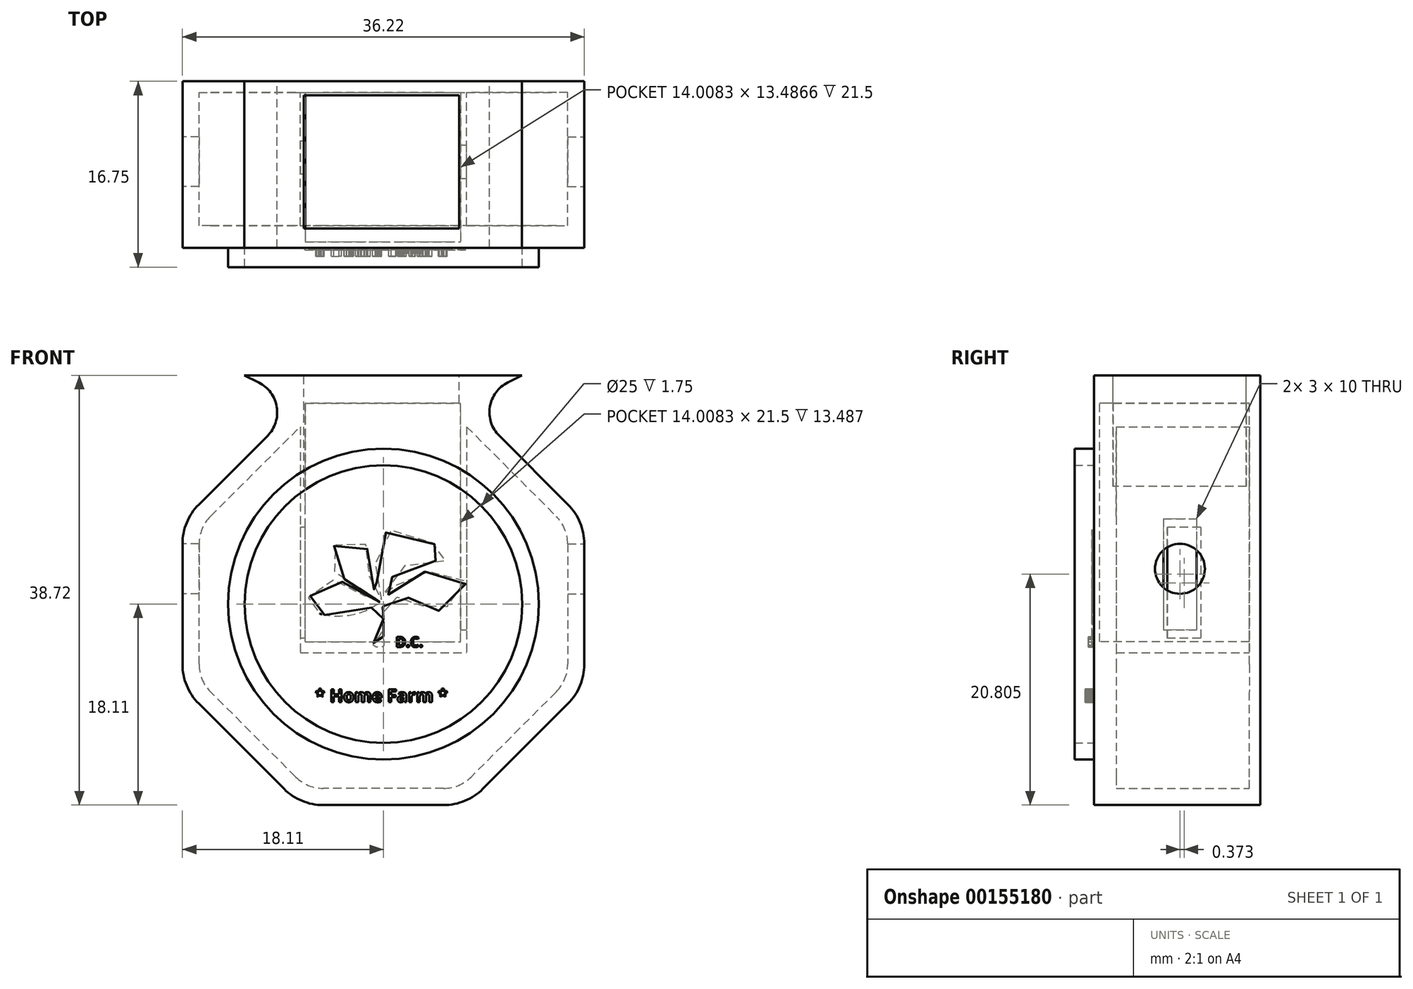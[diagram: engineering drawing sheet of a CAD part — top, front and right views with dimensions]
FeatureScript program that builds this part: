
annotation { "Feature Type Name" : "Feature", "Feature Type Description" : "" }
export const myFeature = defineFeature(function(context is Context, id is Id, definition is map)
    precondition{}
    {
        {
            var Q0;
            Q0=qCreatedBy(makeId("Front.planeOp"),FACE);
            var sketch = newSketch(context, id + "F0", { "sketchPlane" : qUnion([Q0])});
            skCircle(sketch, "E0.cCircle", {"center": v(0, 0) * mm, "radius": 18.1 * mm, "construction": true});
            skLineSegment(sketch, "E0.0", {"start": v(5.43, -18.1) * mm, "end": v(-5.43, -18.1) * mm});
            skLineSegment(sketch, "E0.1", {"start": v(-8.96, -16.64) * mm, "end": v(-16.64, -8.96) * mm});
            skLineSegment(sketch, "E0.2", {"start": v(-18.1, -5.43) * mm, "end": v(-18.1, 5.43) * mm});
            skLineSegment(sketch, "E0.3", {"start": v(-16.64, 8.96) * mm, "end": v(-7.5, 18.1) * mm});
            skLineSegment(sketch, "E0.4", {"start": v(-7.5, 18.1) * mm, "end": v(7.5, 18.1) * mm});
            skLineSegment(sketch, "E0.5", {"start": v(7.5, 18.1) * mm, "end": v(16.64, 8.96) * mm});
            skLineSegment(sketch, "E0.6", {"start": v(18.1, 5.43) * mm, "end": v(18.1, -5.43) * mm});
            skLineSegment(sketch, "E0.7", {"start": v(16.64, -8.96) * mm, "end": v(8.96, -16.64) * mm});
            skPoint(sketch, "E0.0.midPoint", {"position": v(0, -18.1) * mm});
            skPoint(sketch, "E1.visualSharp", {"position": v(7.5, -18.1) * mm});
            skArc(sketch, "E1.filletArc", {"start": v(5.43, -18.1) * mm, "mid": v(7.34, -17.73) * mm, "end": v(8.96, -16.64) * mm});
            skPoint(sketch, "E2.visualSharp", {"position": v(-7.5, -18.1) * mm});
            skArc(sketch, "E2.filletArc", {"start": v(-8.96, -16.64) * mm, "mid": v(-7.34, -17.73) * mm, "end": v(-5.43, -18.1) * mm});
            skPoint(sketch, "E3.visualSharp", {"position": v(-18.1, -7.5) * mm});
            skArc(sketch, "E3.filletArc", {"start": v(-18.1, -5.43) * mm, "mid": v(-17.73, -7.34) * mm, "end": v(-16.64, -8.96) * mm});
            skPoint(sketch, "E4.visualSharp", {"position": v(18.1, -7.5) * mm});
            skArc(sketch, "E4.filletArc", {"start": v(16.64, -8.96) * mm, "mid": v(17.73, -7.34) * mm, "end": v(18.1, -5.43) * mm});
            skPoint(sketch, "E5.visualSharp", {"position": v(18.1, 7.5) * mm});
            skArc(sketch, "E5.filletArc", {"start": v(18.1, 5.43) * mm, "mid": v(17.73, 7.34) * mm, "end": v(16.64, 8.96) * mm});
            skPoint(sketch, "E6.visualSharp", {"position": v(-18.1, 7.5) * mm});
            skArc(sketch, "E6.filletArc", {"start": v(-16.64, 8.96) * mm, "mid": v(-17.73, 7.34) * mm, "end": v(-18.1, 5.43) * mm});
            skLineSegment(sketch, "E7.0", {"start": v(-15.72, 16.6) * mm, "end": v(4.28, 16.6) * mm});
            skSolve(sketch);
        }
        {
            var Q0;
            Q0=makeQuery(id+"F0.imprint","IMPRINT",FACE,{"disambiguationData":[TD([[makeQuery(id+"F0.imprint","IMPRINT",EDGE,{"derivedFrom":sQuery(id+"F0.wireOp",EDGE,"E0.0")}),-1.0]])]});
            extrude(context, id + "F1", {"entities" : qUnion([Q0]), "depth" : 15 * mm});
        }
        {
            var Q0;
            Q0=makeQuery(id+"F1.opExtrude","CAP_FACE",FACE,{"disambiguationData":[OSD([sQuery(id+"F0.wireOp",EDGE,"E0.0"),sQuery(id+"F0.wireOp",EDGE,"E0.1"),sQuery(id+"F0.wireOp",EDGE,"E0.2"),sQuery(id+"F0.wireOp",EDGE,"E0.3"),sQuery(id+"F0.wireOp",EDGE,"E0.4"),sQuery(id+"F0.wireOp",EDGE,"E0.5"),sQuery(id+"F0.wireOp",EDGE,"E0.6"),sQuery(id+"F0.wireOp",EDGE,"E0.7"),sQuery(id+"F0.wireOp",EDGE,"E1.filletArc"),sQuery(id+"F0.wireOp",EDGE,"E2.filletArc"),sQuery(id+"F0.wireOp",EDGE,"E3.filletArc"),sQuery(id+"F0.wireOp",EDGE,"E4.filletArc"),sQuery(id+"F0.wireOp",EDGE,"E5.filletArc"),sQuery(id+"F0.wireOp",EDGE,"E6.filletArc")])],"isStart":false});
            var sketch = newSketch(context, id + "F2", { "sketchPlane" : qUnion([Q0])});
            skCircle(sketch, "E8", {"center": v(0, 0) * mm, "radius": 14 * mm});
            skCircle(sketch, "E9.0", {"center": v(0, 0) * mm, "radius": 12.5 * mm});
            skSolve(sketch);
        }
        {
            var Q0;
            Q0 = qSketchRegion(id + "F2", true);
            extrude(context, id + "F3", {"entities" : qUnion([Q0]), "operationType" : NewBodyOperationType.ADD, "depth" : 1.75 * mm});
        }
        {
            var Q0;
            Q0=makeQuery(id+"F3.boolean.opBoolean","SPLIT",FACE,{"disambiguationData":[TD([makeQuery(id+"F3.opExtrude","SWEPT_FACE",FACE,{"disambiguationData":[OSD([sQuery(id+"F2.wireOp",EDGE,"E9.0")])]})])],"derivedFrom":makeQuery(id+"F1.opExtrude","CAP_FACE",FACE,{"disambiguationData":[OSD([sQuery(id+"F0.wireOp",EDGE,"E0.0"),sQuery(id+"F0.wireOp",EDGE,"E0.1"),sQuery(id+"F0.wireOp",EDGE,"E0.2"),sQuery(id+"F0.wireOp",EDGE,"E0.3"),sQuery(id+"F0.wireOp",EDGE,"E0.4"),sQuery(id+"F0.wireOp",EDGE,"E0.5"),sQuery(id+"F0.wireOp",EDGE,"E0.6"),sQuery(id+"F0.wireOp",EDGE,"E0.7"),sQuery(id+"F0.wireOp",EDGE,"E1.filletArc"),sQuery(id+"F0.wireOp",EDGE,"E2.filletArc"),sQuery(id+"F0.wireOp",EDGE,"E3.filletArc"),sQuery(id+"F0.wireOp",EDGE,"E4.filletArc"),sQuery(id+"F0.wireOp",EDGE,"E5.filletArc"),sQuery(id+"F0.wireOp",EDGE,"E6.filletArc")])],"isStart":false})});
            var sketch = newSketch(context, id + "F4", { "sketchPlane" : qUnion([Q0])});
            skText(sketch, "E10", { "text": "* Home Farm *", "fontName": "OpenSans-Bold.ttf"});
            const initialGuessF4  = {"E10": [-0.00615, -0.00883, 1, 0, 0.00116]};
            skSetInitialGuess(sketch, initialGuessF4);
            skSolve(sketch);
        }
        {
            var Q0;
            Q0 = qSketchRegion(id + "F4", true);
            extrude(context, id + "F5", {"entities" : qUnion([Q0]), "operationType" : NewBodyOperationType.ADD, "depth" : 0.78 * mm});
        }
        {
            var Q0;
            Q0=makeQuery(id+"F1.opExtrude","SWEPT_FACE",FACE,{"disambiguationData":[OSD([sQuery(id+"F0.wireOp",EDGE,"E0.4")])]});
            var sketch = newSketch(context, id + "F6", { "sketchPlane" : qUnion([Q0])});
            skLineSegment(sketch, "E11.bottom", {"start": v(-7.5, 0) * mm, "end": v(7.5, 0) * mm});
            skLineSegment(sketch, "E11.top", {"start": v(-7.5, -15) * mm, "end": v(7.5, -15) * mm});
            skLineSegment(sketch, "E11.left", {"start": v(-7.5, 0) * mm, "end": v(-7.5, -15) * mm});
            skLineSegment(sketch, "E11.right", {"start": v(7.5, 0) * mm, "end": v(7.5, -15) * mm});
            skSolve(sketch);
        }
        {
            var Q0;
            {var subQ0=makeQuery(id+"F3.opExtrude","SWEPT_FACE",FACE,{"disambiguationData":[OSD([sQuery(id+"F2.wireOp",EDGE,"E9.0")])]});Q0=makeQuery(id+"F5.boolean.opBoolean","SPLIT",FACE,{"disambiguationData":[TD([subQ0])],"derivedFrom":makeQuery(id+"F3.boolean.opBoolean","SPLIT",FACE,{"disambiguationData":[TD([subQ0])],"derivedFrom":makeQuery(id+"F1.opExtrude","CAP_FACE",FACE,{"disambiguationData":[OSD([sQuery(id+"F0.wireOp",EDGE,"E0.0"),sQuery(id+"F0.wireOp",EDGE,"E0.1"),sQuery(id+"F0.wireOp",EDGE,"E0.2"),sQuery(id+"F0.wireOp",EDGE,"E0.3"),sQuery(id+"F0.wireOp",EDGE,"E0.4"),sQuery(id+"F0.wireOp",EDGE,"E0.5"),sQuery(id+"F0.wireOp",EDGE,"E0.6"),sQuery(id+"F0.wireOp",EDGE,"E0.7"),sQuery(id+"F0.wireOp",EDGE,"E1.filletArc"),sQuery(id+"F0.wireOp",EDGE,"E2.filletArc"),sQuery(id+"F0.wireOp",EDGE,"E3.filletArc"),sQuery(id+"F0.wireOp",EDGE,"E4.filletArc"),sQuery(id+"F0.wireOp",EDGE,"E5.filletArc"),sQuery(id+"F0.wireOp",EDGE,"E6.filletArc")])],"isStart":false})})});}
            var sketch = newSketch(context, id + "F7", { "sketchPlane" : qUnion([Q0])});
            skFitSpline(sketch, "E12", {"points": [v(0, -2.92) * mm, v(0.28, -1.42) * mm, v(0, 0) * mm, v(1.05, 0.6) * mm, v(2.74, 0.4) * mm, v(4.44, -0.62) * mm, v(6.04, 0) * mm, v(7.38, 2) * mm, v(4.3, 2.93) * mm, v(1.37, 1.93) * mm, v(0, 0.4) * mm, v(0.55, 2.06) * mm, v(3.22, 3.86) * mm, v(6.04, 4.07) * mm, v(3.24, 6.14) * mm, v(0, 6.25) * mm, v(-0.59, 1.86) * mm, v(-0.2, 0.4) * mm, v(-1.13, 2) * mm, v(-1.4, 4.68) * mm, v(-2.23, 5.91) * mm, v(-5.16, 4.48) * mm, v(-3.39, 2.18) * mm, v(-0.27, 0.2) * mm, v(-1.68, 0.74) * mm, v(-4.41, 2.18) * mm, v(-6.33, 0.97) * mm, v(-7.08, 0) * mm, v(-4.96, -1.03) * mm, v(-1.23, -0.42) * mm, v(-0.34, 0) * mm, v(0, -1.1) * mm, v(0, -1.62) * mm, v(-0.31, -2.8) * mm, v(-0.93, -3.7) * mm, v(0, -3.81) * mm, v(0, -2.92) * mm]});
            skSolve(sketch);
        }
        {
            var Q0;
            Q0=makeQuery(id+"F7.imprint","IMPRINT",FACE,{"disambiguationData":[TD([[makeQuery(id+"F7.imprint","IMPRINT",EDGE,{"derivedFrom":sQuery(id+"F7.wireOp",EDGE,"E12")}),1.0]])]});
            extrude(context, id + "F8", {"entities" : qUnion([Q0]), "operationType" : NewBodyOperationType.ADD, "depth" : 0.2 * mm});
        }
        {
            var Q0;
            {var subQ0=makeQuery(id+"F3.opExtrude","SWEPT_FACE",FACE,{"disambiguationData":[OSD([sQuery(id+"F2.wireOp",EDGE,"E9.0")])]});Q0=makeQuery(id+"F5.boolean.opBoolean","SPLIT",FACE,{"disambiguationData":[TD([subQ0])],"derivedFrom":makeQuery(id+"F3.boolean.opBoolean","SPLIT",FACE,{"disambiguationData":[TD([subQ0])],"derivedFrom":makeQuery(id+"F1.opExtrude","CAP_FACE",FACE,{"disambiguationData":[OSD([sQuery(id+"F0.wireOp",EDGE,"E0.0"),sQuery(id+"F0.wireOp",EDGE,"E0.1"),sQuery(id+"F0.wireOp",EDGE,"E0.2"),sQuery(id+"F0.wireOp",EDGE,"E0.3"),sQuery(id+"F0.wireOp",EDGE,"E0.4"),sQuery(id+"F0.wireOp",EDGE,"E0.5"),sQuery(id+"F0.wireOp",EDGE,"E0.6"),sQuery(id+"F0.wireOp",EDGE,"E0.7"),sQuery(id+"F0.wireOp",EDGE,"E1.filletArc"),sQuery(id+"F0.wireOp",EDGE,"E2.filletArc"),sQuery(id+"F0.wireOp",EDGE,"E3.filletArc"),sQuery(id+"F0.wireOp",EDGE,"E4.filletArc"),sQuery(id+"F0.wireOp",EDGE,"E5.filletArc"),sQuery(id+"F0.wireOp",EDGE,"E6.filletArc")])],"isStart":false})})});}
            var sketch = newSketch(context, id + "F9", { "sketchPlane" : qUnion([Q0])});
            skText(sketch, "E13", { "text": "D.C.", "fontName": "OpenSans-Bold.ttf"});
            const initialGuessF9  = {"E13": [0.00109, -0.00387, 1, 0, 0.00092]};
            skSetInitialGuess(sketch, initialGuessF9);
            skSolve(sketch);
        }
        {
            var Q0;
            Q0 = qSketchRegion(id + "F9", true);
            extrude(context, id + "F10", {"entities" : qUnion([Q0]), "operationType" : NewBodyOperationType.ADD, "depth" : 0.5 * mm});
        }
        {
            var Q0;
            Q0=makeQuery(id+"F1.opExtrude","CAP_FACE",FACE,{"disambiguationData":[OSD([sQuery(id+"F0.wireOp",EDGE,"E0.0"),sQuery(id+"F0.wireOp",EDGE,"E0.1"),sQuery(id+"F0.wireOp",EDGE,"E0.2"),sQuery(id+"F0.wireOp",EDGE,"E0.3"),sQuery(id+"F0.wireOp",EDGE,"E0.4"),sQuery(id+"F0.wireOp",EDGE,"E0.5"),sQuery(id+"F0.wireOp",EDGE,"E0.6"),sQuery(id+"F0.wireOp",EDGE,"E0.7"),sQuery(id+"F0.wireOp",EDGE,"E1.filletArc"),sQuery(id+"F0.wireOp",EDGE,"E2.filletArc"),sQuery(id+"F0.wireOp",EDGE,"E3.filletArc"),sQuery(id+"F0.wireOp",EDGE,"E4.filletArc"),sQuery(id+"F0.wireOp",EDGE,"E5.filletArc"),sQuery(id+"F0.wireOp",EDGE,"E6.filletArc")])],"isStart":true});
            var sketch = newSketch(context, id + "F11", { "sketchPlane" : qUnion([Q0])});
            skArc(sketch, "E14.0", {"start": v(-7.9, -15.58) * mm, "mid": v(-6.77, -16.34) * mm, "end": v(-5.43, -16.6) * mm});
            skLineSegment(sketch, "E14.1", {"start": v(-15.58, -7.9) * mm, "end": v(-7.9, -15.58) * mm});
            skArc(sketch, "E14.2", {"start": v(-16.6, -5.43) * mm, "mid": v(-16.34, -6.77) * mm, "end": v(-15.58, -7.9) * mm});
            skLineSegment(sketch, "E14.3", {"start": v(16.6, -5.43) * mm, "end": v(16.6, 5.43) * mm});
            skArc(sketch, "E14.4", {"start": v(15.58, -7.9) * mm, "mid": v(16.34, -6.77) * mm, "end": v(16.6, -5.43) * mm});
            skLineSegment(sketch, "E14.5", {"start": v(7.9, -15.58) * mm, "end": v(15.58, -7.9) * mm});
            skArc(sketch, "E14.6", {"start": v(5.43, -16.6) * mm, "mid": v(6.77, -16.34) * mm, "end": v(7.9, -15.58) * mm});
            skArc(sketch, "E14.7", {"start": v(16.6, 5.43) * mm, "mid": v(16.34, 6.77) * mm, "end": v(15.58, 7.9) * mm});
            skLineSegment(sketch, "E14.8", {"start": v(15.58, 7.9) * mm, "end": v(6.88, 16.6) * mm});
            skLineSegment(sketch, "E14.9", {"start": v(6.88, 16.6) * mm, "end": v(-6.88, 16.6) * mm});
            skLineSegment(sketch, "E14.10", {"start": v(-5.43, -16.6) * mm, "end": v(5.43, -16.6) * mm});
            skLineSegment(sketch, "E14.11", {"start": v(-6.88, 16.6) * mm, "end": v(-15.58, 7.9) * mm});
            skArc(sketch, "E14.12", {"start": v(-15.58, 7.9) * mm, "mid": v(-16.34, 6.77) * mm, "end": v(-16.6, 5.43) * mm});
            skLineSegment(sketch, "E14.13", {"start": v(-16.6, 5.43) * mm, "end": v(-16.6, -5.43) * mm});
            skSolve(sketch);
        }
        {
            var Q0;
            Q0=makeQuery(id+"F11.imprint","IMPRINT",FACE,{"disambiguationData":[TD([[makeQuery(id+"F11.imprint","IMPRINT",EDGE,{"derivedFrom":sQuery(id+"F11.wireOp",EDGE,"E14.0")}),1.0]])]});
            extrude(context, id + "F12", {"entities" : qUnion([Q0]), "operationType" : NewBodyOperationType.REMOVE, "oppositeDirection" : true, "depth" : 13 * mm});
        }
        {
            var Q0;
            Q0=makeQuery(id+"F6.imprint","IMPRINT",FACE,{"disambiguationData":[TD([[makeQuery(id+"F6.imprint","IMPRINT",EDGE,{"derivedFrom":sQuery(id+"F6.wireOp",EDGE,"E11.bottom")}),-1.0]])]});
            extrude(context, id + "F13", {"entities" : qUnion([Q0]), "operationType" : NewBodyOperationType.ADD, "oppositeDirection" : true, "depth" : 22.5 * mm});
        }
        {
            var Q0;
            Q0=makeQuery(id+"F1.opExtrude","SWEPT_FACE",FACE,{"disambiguationData":[OSD([sQuery(id+"F0.wireOp",EDGE,"E0.4")])]});
            var sketch = newSketch(context, id + "F14", { "sketchPlane" : qUnion([Q0])});
            skLineSegment(sketch, "E15.bottom", {"start": v(-7.04, -0.51) * mm, "end": v(6.97, -0.51) * mm});
            skLineSegment(sketch, "E15.top", {"start": v(-7.04, -14.49) * mm, "end": v(6.97, -14.49) * mm});
            skLineSegment(sketch, "E15.left", {"start": v(-7.04, -0.51) * mm, "end": v(-7.04, -14.49) * mm});
            skLineSegment(sketch, "E15.right", {"start": v(6.97, -0.51) * mm, "end": v(6.97, -14.49) * mm});
            skSolve(sketch);
        }
        {
            var Q0;
            Q0=makeQuery(id+"F13.boolean.opBoolean","MERGE",FACE,{"derivedFrom":[makeQuery(id+"F1.opExtrude","CAP_FACE",FACE,{"disambiguationData":[OSD([sQuery(id+"F0.wireOp",EDGE,"E0.0"),sQuery(id+"F0.wireOp",EDGE,"E0.1"),sQuery(id+"F0.wireOp",EDGE,"E0.2"),sQuery(id+"F0.wireOp",EDGE,"E0.3"),sQuery(id+"F0.wireOp",EDGE,"E0.4"),sQuery(id+"F0.wireOp",EDGE,"E0.5"),sQuery(id+"F0.wireOp",EDGE,"E0.6"),sQuery(id+"F0.wireOp",EDGE,"E0.7"),sQuery(id+"F0.wireOp",EDGE,"E1.filletArc"),sQuery(id+"F0.wireOp",EDGE,"E2.filletArc"),sQuery(id+"F0.wireOp",EDGE,"E3.filletArc"),sQuery(id+"F0.wireOp",EDGE,"E4.filletArc"),sQuery(id+"F0.wireOp",EDGE,"E5.filletArc"),sQuery(id+"F0.wireOp",EDGE,"E6.filletArc")])],"isStart":true}),makeQuery(id+"F13.opExtrude","SWEPT_FACE",FACE,{"disambiguationData":[OSD([sQuery(id+"F6.wireOp",EDGE,"E11.bottom")])]})]});
            var sketch = newSketch(context, id + "F15", { "sketchPlane" : qUnion([Q0])});
            skLineSegment(sketch, "E16.bottom", {"start": v(-6.35, 12.73) * mm, "end": v(6.65, 12.73) * mm});
            skLineSegment(sketch, "E16.top", {"start": v(-6.35, 11.73) * mm, "end": v(6.65, 11.73) * mm});
            skLineSegment(sketch, "E16.left", {"start": v(-6.35, 12.73) * mm, "end": v(-6.35, 11.73) * mm});
            skLineSegment(sketch, "E16.right", {"start": v(6.65, 12.73) * mm, "end": v(6.65, 11.73) * mm});
            skLineSegment(sketch, "E17.bottom", {"start": v(-6.35, 9.52) * mm, "end": v(6.65, 9.52) * mm});
            skLineSegment(sketch, "E17.top", {"start": v(-6.35, 8.13) * mm, "end": v(6.65, 8.13) * mm});
            skLineSegment(sketch, "E17.left", {"start": v(-6.35, 9.52) * mm, "end": v(-6.35, 8.13) * mm});
            skLineSegment(sketch, "E17.right", {"start": v(6.65, 9.52) * mm, "end": v(6.65, 8.13) * mm});
            skLineSegment(sketch, "E18.bottom", {"start": v(-6.35, 5.8) * mm, "end": v(6.65, 5.8) * mm});
            skLineSegment(sketch, "E18.top", {"start": v(-6.35, 4.38) * mm, "end": v(6.65, 4.38) * mm});
            skLineSegment(sketch, "E18.left", {"start": v(-6.35, 5.8) * mm, "end": v(-6.35, 4.38) * mm});
            skLineSegment(sketch, "E18.right", {"start": v(6.65, 5.8) * mm, "end": v(6.65, 4.38) * mm});
            skLineSegment(sketch, "E19.bottom", {"start": v(-6.38, 2.26) * mm, "end": v(6.62, 2.26) * mm});
            skLineSegment(sketch, "E19.top", {"start": v(-6.38, 0.78) * mm, "end": v(6.62, 0.78) * mm});
            skLineSegment(sketch, "E19.left", {"start": v(-6.38, 2.26) * mm, "end": v(-6.38, 0.78) * mm});
            skLineSegment(sketch, "E19.right", {"start": v(6.62, 2.26) * mm, "end": v(6.62, 0.78) * mm});
            skLineSegment(sketch, "E20.bottom", {"start": v(-6.24, -1.06) * mm, "end": v(6.76, -1.06) * mm});
            skLineSegment(sketch, "E20.top", {"start": v(-6.24, -2.36) * mm, "end": v(6.76, -2.36) * mm});
            skLineSegment(sketch, "E20.left", {"start": v(-6.24, -1.06) * mm, "end": v(-6.24, -2.36) * mm});
            skLineSegment(sketch, "E20.right", {"start": v(6.76, -1.06) * mm, "end": v(6.76, -2.36) * mm});
            skSolve(sketch);
        }
        {
            var Q0;
            Q0=makeQuery(id+"F15.imprint","IMPRINT",FACE,{"disambiguationData":[TD([[makeQuery(id+"F15.imprint","IMPRINT",EDGE,{"derivedFrom":sQuery(id+"F15.wireOp",EDGE,"E16.bottom")}),-1.0]])]});
            var Q1;
            Q1=makeQuery(id+"F15.imprint","IMPRINT",FACE,{"disambiguationData":[TD([[makeQuery(id+"F15.imprint","IMPRINT",EDGE,{"derivedFrom":sQuery(id+"F15.wireOp",EDGE,"E17.bottom")}),-1.0]])]});
            var Q2;
            Q2=makeQuery(id+"F15.imprint","IMPRINT",FACE,{"disambiguationData":[TD([[makeQuery(id+"F15.imprint","IMPRINT",EDGE,{"derivedFrom":sQuery(id+"F15.wireOp",EDGE,"E18.bottom")}),-1.0]])]});
            var Q3;
            Q3=makeQuery(id+"F15.imprint","IMPRINT",FACE,{"disambiguationData":[TD([[makeQuery(id+"F15.imprint","IMPRINT",EDGE,{"derivedFrom":sQuery(id+"F15.wireOp",EDGE,"E19.bottom")}),-1.0]])]});
            var Q4;
            Q4=makeQuery(id+"F15.imprint","IMPRINT",FACE,{"disambiguationData":[TD([[makeQuery(id+"F15.imprint","IMPRINT",EDGE,{"derivedFrom":sQuery(id+"F15.wireOp",EDGE,"E20.bottom")}),-1.0]])]});
            extrude(context, id + "F16", {"entities" : qUnion([Q0, Q1, Q2, Q3, Q4]), "operationType" : NewBodyOperationType.REMOVE, "oppositeDirection" : true, "depth" : 10 * mm});
        }
        {
            var Q0;
            Q0=makeQuery(id+"F13.opExtrude","SWEPT_FACE",FACE,{"disambiguationData":[OSD([sQuery(id+"F6.wireOp",EDGE,"E11.right")])]});
            var sketch = newSketch(context, id + "F17", { "sketchPlane" : qUnion([Q0])});
            skLineSegment(sketch, "E21.bottom", {"start": v(-8.75, 7.7) * mm, "end": v(-5.75, 7.7) * mm});
            skLineSegment(sketch, "E21.top", {"start": v(-8.75, -2.3) * mm, "end": v(-5.75, -2.3) * mm});
            skLineSegment(sketch, "E21.left", {"start": v(-8.75, 7.7) * mm, "end": v(-8.75, -2.3) * mm});
            skLineSegment(sketch, "E21.right", {"start": v(-5.75, 7.7) * mm, "end": v(-5.75, -2.3) * mm});
            skSolve(sketch);
        }
        {
            var Q0;
            Q0=makeQuery(id+"F17.imprint","IMPRINT",FACE,{"disambiguationData":[TD([[makeQuery(id+"F17.imprint","IMPRINT",EDGE,{"derivedFrom":sQuery(id+"F17.wireOp",EDGE,"E21.bottom")}),-1.0]])]});
            extrude(context, id + "F18", {"entities" : qUnion([Q0]), "operationType" : NewBodyOperationType.REMOVE, "oppositeDirection" : true, "depth" : 5 * mm});
        }
        {
            var Q0;
            Q0=makeQuery(id+"F13.opExtrude","SWEPT_FACE",FACE,{"disambiguationData":[OSD([sQuery(id+"F6.wireOp",EDGE,"E11.left")])]});
            var sketch = newSketch(context, id + "F19", { "sketchPlane" : qUnion([Q0])});
            skLineSegment(sketch, "E22.bottom", {"start": v(5.38, 6.9) * mm, "end": v(8.38, 6.9) * mm});
            skLineSegment(sketch, "E22.top", {"start": v(5.38, -3.1) * mm, "end": v(8.38, -3.1) * mm});
            skLineSegment(sketch, "E22.left", {"start": v(5.38, 6.9) * mm, "end": v(5.38, -3.1) * mm});
            skLineSegment(sketch, "E22.right", {"start": v(8.38, 6.9) * mm, "end": v(8.38, -3.1) * mm});
            skSolve(sketch);
        }
        {
            var Q0;
            Q0=makeQuery(id+"F19.imprint","IMPRINT",FACE,{"disambiguationData":[TD([[makeQuery(id+"F19.imprint","IMPRINT",EDGE,{"derivedFrom":sQuery(id+"F19.wireOp",EDGE,"E22.bottom")}),-1.0]])]});
            extrude(context, id + "F20", {"entities" : qUnion([Q0]), "operationType" : NewBodyOperationType.REMOVE, "oppositeDirection" : true, "depth" : 5 * mm});
        }
        {
            var Q0;
            Q0=makeQuery(id+"F1.opExtrude","SWEPT_FACE",FACE,{"disambiguationData":[OSD([sQuery(id+"F0.wireOp",EDGE,"E0.6")])]});
            var sketch = newSketch(context, id + "F21", { "sketchPlane" : qUnion([Q0])});
            skCircle(sketch, "E23", {"center": v(-7.25, 3.18) * mm, "radius": 2.25 * mm});
            skSolve(sketch);
        }
        {
            var Q0;
            Q0=makeQuery(id+"F21.imprint","IMPRINT",FACE,{"disambiguationData":[TD([[makeQuery(id+"F21.imprint","IMPRINT",EDGE,{"derivedFrom":sQuery(id+"F21.wireOp",EDGE,"E23")}),1.0]])]});
            extrude(context, id + "F22", {"entities" : qUnion([Q0]), "operationType" : NewBodyOperationType.REMOVE, "oppositeDirection" : true, "depth" : 10 * mm});
        }
        {
            var Q0;
            Q0=makeQuery(id+"F1.opExtrude","SWEPT_FACE",FACE,{"disambiguationData":[OSD([sQuery(id+"F0.wireOp",EDGE,"E0.2")])]});
            var sketch = newSketch(context, id + "F23", { "sketchPlane" : qUnion([Q0])});
            skCircle(sketch, "E24", {"center": v(7.25, 3.18) * mm, "radius": 2.25 * mm});
            skSolve(sketch);
        }
        {
            var Q0;
            Q0=makeQuery(id+"F23.imprint","IMPRINT",FACE,{"disambiguationData":[TD([[makeQuery(id+"F23.imprint","IMPRINT",EDGE,{"derivedFrom":sQuery(id+"F23.wireOp",EDGE,"E24")}),1.0]])]});
            extrude(context, id + "F24", {"entities" : qUnion([Q0]), "operationType" : NewBodyOperationType.REMOVE, "oppositeDirection" : true, "depth" : 10 * mm});
        }
        {
            var Q0;
            {var subQ0=sQuery(id+"F0.wireOp",EDGE,"E2.filletArc");var subQ1=sQuery(id+"F0.wireOp",EDGE,"E0.7");var subQ2=sQuery(id+"F0.wireOp",EDGE,"E0.6");var subQ3=sQuery(id+"F0.wireOp",EDGE,"E0.5");var subQ4=sQuery(id+"F0.wireOp",EDGE,"E0.4");var subQ5=sQuery(id+"F0.wireOp",EDGE,"E0.0");var subQ6=sQuery(id+"F0.wireOp",EDGE,"E1.filletArc");var subQ7=sQuery(id+"F0.wireOp",EDGE,"E0.1");var subQ8=sQuery(id+"F0.wireOp",EDGE,"E0.2");var subQ9=sQuery(id+"F0.wireOp",EDGE,"E0.3");var subQ10=sQuery(id+"F0.wireOp",EDGE,"E3.filletArc");var subQ11=sQuery(id+"F0.wireOp",EDGE,"E4.filletArc");var subQ12=sQuery(id+"F0.wireOp",EDGE,"E5.filletArc");var subQ13=sQuery(id+"F0.wireOp",EDGE,"E6.filletArc");Q0=makeQuery(id+"F3.boolean.opBoolean","SPLIT",FACE,{"disambiguationData":[TD([makeQuery(id+"F1.opExtrude","SWEPT_FACE",FACE,{"disambiguationData":[OSD([subQ5])]})])],"derivedFrom":makeQuery(id+"F1.opExtrude","CAP_FACE",FACE,{"disambiguationData":[OSD([subQ5,subQ7,subQ8,subQ9,subQ4,subQ3,subQ2,subQ1,subQ6,subQ0,subQ10,subQ11,subQ12,subQ13])],"isStart":false})});}
            var sketch = newSketch(context, id + "F25", { "sketchPlane" : qUnion([Q0])});
            skLineSegment(sketch, "E25", {"start": v(-12.53, 20.6) * mm, "end": v(12.47, 20.6) * mm});
            skLineSegment(sketch, "E26", {"start": v(12.47, 20.6) * mm, "end": v(7.5, 18.1) * mm});
            skLineSegment(sketch, "E27", {"start": v(7.5, 18.1) * mm, "end": v(-7.5, 18.1) * mm});
            skLineSegment(sketch, "E28", {"start": v(-7.5, 18.1) * mm, "end": v(-12.53, 20.6) * mm});
            skSolve(sketch);
        }
        {
            var Q0;
            Q0=makeQuery(id+"F25.imprint","IMPRINT",FACE,{"disambiguationData":[TD([[makeQuery(id+"F25.imprint","IMPRINT",EDGE,{"derivedFrom":sQuery(id+"F25.wireOp",EDGE,"E25")}),-1.0]])]});
            extrude(context, id + "F26", {"entities" : qUnion([Q0]), "operationType" : NewBodyOperationType.ADD, "oppositeDirection" : true, "depth" : 15 * mm});
        }
        {
            var Q0;
            {var subQ0=sQuery(id+"F0.wireOp",EDGE,"E0.5");Q0=makeQuery(id+"F26.boolean.opBoolean","MERGE",EDGE,{"derivedFrom":[makeQuery(id+"F1.opExtrude","SWEPT_EDGE",EDGE,{"disambiguationData":[OSD([sQuery(id+"F0.wireOp",EDGE,"E0.4"),subQ0])]}),makeQuery(id+"F26.opExtrude","SWEPT_EDGE",EDGE,{"disambiguationData":[OSD([subQ0,sQuery(id+"F25.wireOp",EDGE,"E26"),sQuery(id+"F25.wireOp",EDGE,"E27")])]})]});}
            fillet(context, id + "F27", {"entities" : qUnion([Q0]), "radius" : 3 * mm, "tangentPropagation" : true, "allowEdgeOverflow" : false});
        }
        {
            var Q0;
            {var subQ0=sQuery(id+"F0.wireOp",EDGE,"E0.3");Q0=makeQuery(id+"F26.boolean.opBoolean","MERGE",EDGE,{"derivedFrom":[makeQuery(id+"F1.opExtrude","SWEPT_EDGE",EDGE,{"disambiguationData":[OSD([subQ0,sQuery(id+"F0.wireOp",EDGE,"E0.4")])]}),makeQuery(id+"F26.opExtrude","SWEPT_EDGE",EDGE,{"disambiguationData":[OSD([subQ0,sQuery(id+"F25.wireOp",EDGE,"E27"),sQuery(id+"F25.wireOp",EDGE,"E28")])]})]});}
            fillet(context, id + "F28", {"entities" : qUnion([Q0]), "radius" : 3 * mm, "tangentPropagation" : true, "allowEdgeOverflow" : false});
        }
        {
            var Q0;
            Q0=makeQuery(id+"F26.opExtrude","SWEPT_FACE",FACE,{"disambiguationData":[OSD([sQuery(id+"F25.wireOp",EDGE,"E25")])]});
            var sketch = newSketch(context, id + "F29", { "sketchPlane" : qUnion([Q0])});
            skLineSegment(sketch, "E29.bottom", {"start": v(-7.17, -1.28) * mm, "end": v(6.83, -1.28) * mm});
            skLineSegment(sketch, "E29.top", {"start": v(-7.17, -13.28) * mm, "end": v(6.83, -13.28) * mm});
            skLineSegment(sketch, "E29.left", {"start": v(-7.17, -1.28) * mm, "end": v(-7.17, -13.28) * mm});
            skLineSegment(sketch, "E29.right", {"start": v(6.83, -1.28) * mm, "end": v(6.83, -13.28) * mm});
            skSolve(sketch);
        }
        {
            var Q0;
            Q0=makeQuery(id+"F29.imprint","IMPRINT",FACE,{"disambiguationData":[TD([[makeQuery(id+"F29.imprint","IMPRINT",EDGE,{"derivedFrom":sQuery(id+"F29.wireOp",EDGE,"Z295dryF-vfGy-lkrf-hUhb-PSniFN7pxlop.bottom")}),-1.0]])]});
            var Q1;
            Q1=makeQuery(id+"F29.imprint","IMPRINT",FACE,{"disambiguationData":[TD([[makeQuery(id+"F29.imprint","IMPRINT",EDGE,{"derivedFrom":sQuery(id+"F29.wireOp",EDGE,"E29.bottom")}),-1.0]])]});
            var Q2;
            Q2=sQuery(id+"F29.wireOp",EDGE,"Z295dryF-vfGy-lkrf-hUhb-PSniFN7pxlop.right");
            extrude(context, id + "F30", {"entities" : qUnion([Q0, Q1]), "operationType" : NewBodyOperationType.REMOVE, "surfaceEntities" : qUnion([Q2]), "oppositeDirection" : true, "depth" : 10 * mm});
        }
        {
            var Q0;
            Q0=makeQuery(id+"F14.imprint","IMPRINT",FACE,{"disambiguationData":[TD([[makeQuery(id+"F14.imprint","IMPRINT",EDGE,{"derivedFrom":sQuery(id+"F14.wireOp",EDGE,"E15.bottom")}),-1.0]])]});
            extrude(context, id + "F31", {"entities" : qUnion([Q0]), "operationType" : NewBodyOperationType.REMOVE, "oppositeDirection" : true, "depth" : 21.5 * mm});
        }
        {
            var Q0;
            Q0=qCreatedBy(makeId("Front.planeOp"),FACE);
            var sketch = newSketch(context, id + "F32", { "sketchPlane" : qUnion([Q0])});
            skCircle(sketch, "E30.cCircle", {"center": v(0, 0) * mm, "radius": 18.1 * mm, "construction": true});
            skLineSegment(sketch, "E30.0", {"start": v(5.43, -18.1) * mm, "end": v(-5.43, -18.1) * mm});
            skLineSegment(sketch, "E30.1", {"start": v(-8.96, -16.64) * mm, "end": v(-16.64, -8.96) * mm});
            skLineSegment(sketch, "E30.2", {"start": v(-18.1, -5.43) * mm, "end": v(-18.1, 5.43) * mm});
            skLineSegment(sketch, "E30.3", {"start": v(-16.64, 8.96) * mm, "end": v(-7.5, 18.1) * mm});
            skLineSegment(sketch, "E30.4", {"start": v(-7.5, 18.1) * mm, "end": v(7.5, 18.1) * mm});
            skLineSegment(sketch, "E30.5", {"start": v(7.5, 18.1) * mm, "end": v(16.64, 8.96) * mm});
            skLineSegment(sketch, "E30.6", {"start": v(18.1, 5.43) * mm, "end": v(18.1, -5.43) * mm});
            skLineSegment(sketch, "E30.7", {"start": v(16.64, -8.96) * mm, "end": v(8.96, -16.64) * mm});
            skPoint(sketch, "E30.0.midPoint", {"position": v(0, -18.1) * mm});
            skPoint(sketch, "E31.visualSharp", {"position": v(7.5, -18.1) * mm});
            skArc(sketch, "E31.filletArc", {"start": v(5.43, -18.1) * mm, "mid": v(7.34, -17.73) * mm, "end": v(8.96, -16.64) * mm});
            skPoint(sketch, "E32.visualSharp", {"position": v(-7.5, -18.1) * mm});
            skArc(sketch, "E32.filletArc", {"start": v(-8.96, -16.64) * mm, "mid": v(-7.34, -17.73) * mm, "end": v(-5.43, -18.1) * mm});
            skPoint(sketch, "E33.visualSharp", {"position": v(-18.1, -7.5) * mm});
            skArc(sketch, "E33.filletArc", {"start": v(-18.1, -5.43) * mm, "mid": v(-17.73, -7.34) * mm, "end": v(-16.64, -8.96) * mm});
            skPoint(sketch, "E34.visualSharp", {"position": v(18.1, -7.5) * mm});
            skArc(sketch, "E34.filletArc", {"start": v(16.64, -8.96) * mm, "mid": v(17.73, -7.34) * mm, "end": v(18.1, -5.43) * mm});
            skPoint(sketch, "E35.visualSharp", {"position": v(18.1, 7.5) * mm});
            skArc(sketch, "E35.filletArc", {"start": v(18.1, 5.43) * mm, "mid": v(17.73, 7.34) * mm, "end": v(16.64, 8.96) * mm});
            skPoint(sketch, "E36.visualSharp", {"position": v(-18.1, 7.5) * mm});
            skArc(sketch, "E36.filletArc", {"start": v(-16.64, 8.96) * mm, "mid": v(-17.73, 7.34) * mm, "end": v(-18.1, 5.43) * mm});
            skLineSegment(sketch, "E37.0", {"start": v(-15.47, 16.6) * mm, "end": v(4.53, 16.6) * mm});
            skSolve(sketch);
        }
        {
            var Q0;
            Q0 = qSketchRegion(id + "F32", true);
            extrude(context, id + "F33", {"entities" : qUnion([Q0]), "operationType" : NewBodyOperationType.ADD, "depth" : 1 * mm});
        }
    });
